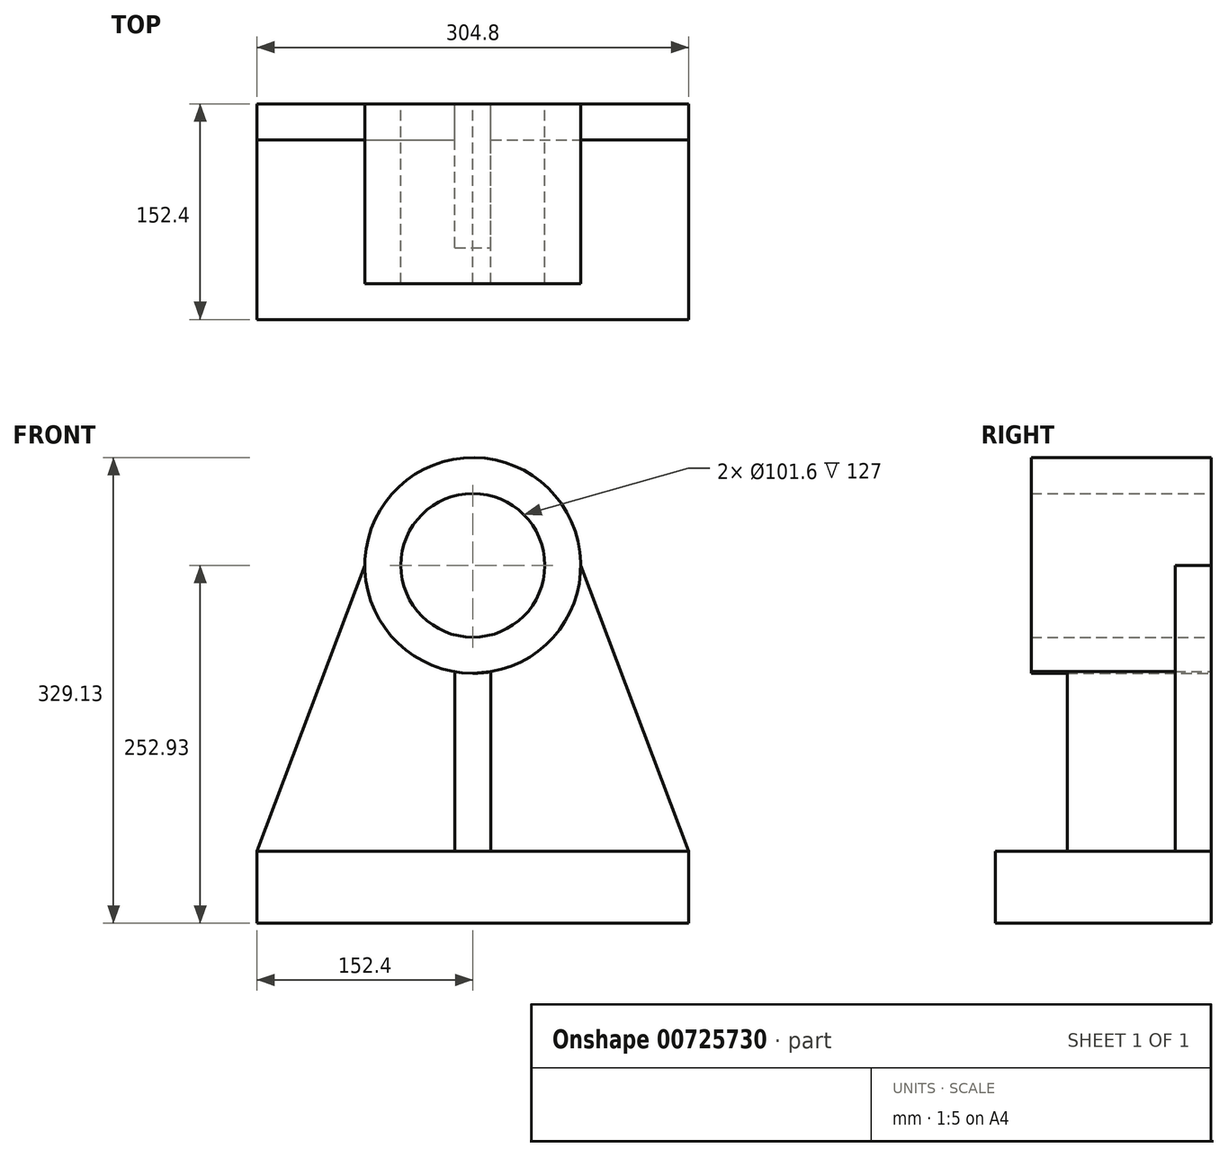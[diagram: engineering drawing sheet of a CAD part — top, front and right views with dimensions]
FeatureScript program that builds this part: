
annotation { "Feature Type Name" : "Feature", "Feature Type Description" : "" }
export const myFeature = defineFeature(function(context is Context, id is Id, definition is map)
    precondition{}
    {
        {
            var Q0;
            Q0=qCreatedBy(makeId("Front.planeOp"),FACE);
            var sketch = newSketch(context, id + "F0", { "sketchPlane" : qUnion([Q0])});
            skCircle(sketch, "E0", {"center": v(0, 0) * mm, "radius": 76.2 * mm});
            skCircle(sketch, "E1", {"center": v(0, 0) * mm, "radius": 50.8 * mm});
            skLineSegment(sketch, "E2", {"start": v(0, -76.2) * mm, "end": v(12.7, -75.13) * mm});
            skLineSegment(sketch, "E3", {"start": v(12.7, -75.13) * mm, "end": v(12.7, -202.13) * mm});
            skLineSegment(sketch, "E4", {"start": v(12.7, -202.13) * mm, "end": v(152.4, -202.13) * mm});
            skLineSegment(sketch, "E5", {"start": v(152.4, -202.13) * mm, "end": v(152.4, -252.93) * mm});
            skLineSegment(sketch, "E6", {"start": v(152.4, -252.93) * mm, "end": v(-152.4, -252.93) * mm});
            skLineSegment(sketch, "E7", {"start": v(-152.4, -252.93) * mm, "end": v(-152.4, -202.13) * mm});
            skLineSegment(sketch, "E8", {"start": v(-152.4, -202.13) * mm, "end": v(-12.7, -202.13) * mm});
            skLineSegment(sketch, "E9", {"start": v(-12.7, -202.13) * mm, "end": v(-12.7, -75.13) * mm});
            skLineSegment(sketch, "E10", {"start": v(-12.7, -202.13) * mm, "end": v(12.7, -202.13) * mm});
            skLineSegment(sketch, "E11", {"start": v(-76.2, 0) * mm, "end": v(-152.4, -202.13) * mm});
            skLineSegment(sketch, "E12", {"start": v(76.2, 0) * mm, "end": v(152.4, -202.13) * mm});
            skSolve(sketch);
        }
        {
            var Q0;
            Q0=makeQuery(id+"F0.imprint","IMPRINT",FACE,{"disambiguationData":[TD([[makeQuery(id+"F0.imprint","IMPRINT",EDGE,{"derivedFrom":sQuery(id+"F0.wireOp",EDGE,"E4")}),-1.0]])]});
            extrude(context, id + "F1", {"entities" : qUnion([Q0]), "depth" : 152.4 * mm, "offsetDistance" : 25.4 * mm});
        }
        {
            var Q0;
            Q0=makeQuery(id+"F0.imprint","IMPRINT",FACE,{"disambiguationData":[TD([[makeQuery(id+"F0.imprint","IMPRINT",EDGE,{"derivedFrom":sQuery(id+"F0.wireOp",EDGE,"E1")}),-1.0]])]});
            extrude(context, id + "F2", {"entities" : qUnion([Q0]), "depth" : 127 * mm, "offsetDistance" : 25.4 * mm});
        }
        {
            var Q0;
            {var subQ4=sQuery(id+"F0.wireOp",EDGE,"E3");Q0=makeQuery(id+"F0.imprint","IMPRINT",FACE,{"disambiguationData":[TD([[makeQuery(id+"F0.imprint","IMPRINT",EDGE,{"derivedFrom":subQ4}),-1.0]])]});}
            extrude(context, id + "F3", {"entities" : qUnion([Q0]), "depth" : 101.6 * mm, "offsetDistance" : 25.4 * mm});
        }
        {
            var Q0;
            Q0=makeQuery(id+"F0.imprint","IMPRINT",FACE,{"disambiguationData":[TD([[makeQuery(id+"F0.imprint","IMPRINT",EDGE,{"derivedFrom":sQuery(id+"F0.wireOp",EDGE,"E8")}),1.0]])]});
            extrude(context, id + "F4", {"entities" : qUnion([Q0]), "depth" : 25.4 * mm, "offsetDistance" : 25.4 * mm});
        }
        {
            var Q0;
            {var subQ0=sQuery(id+"F0.wireOp",EDGE,"E3");Q0=makeQuery(id+"F0.imprint","IMPRINT",FACE,{"disambiguationData":[TD([[makeQuery(id+"F0.imprint","IMPRINT",EDGE,{"derivedFrom":subQ0}),1.0]])]});}
            extrude(context, id + "F5", {"entities" : qUnion([Q0]), "depth" : 25.4 * mm, "offsetDistance" : 25.4 * mm});
        }
    });
